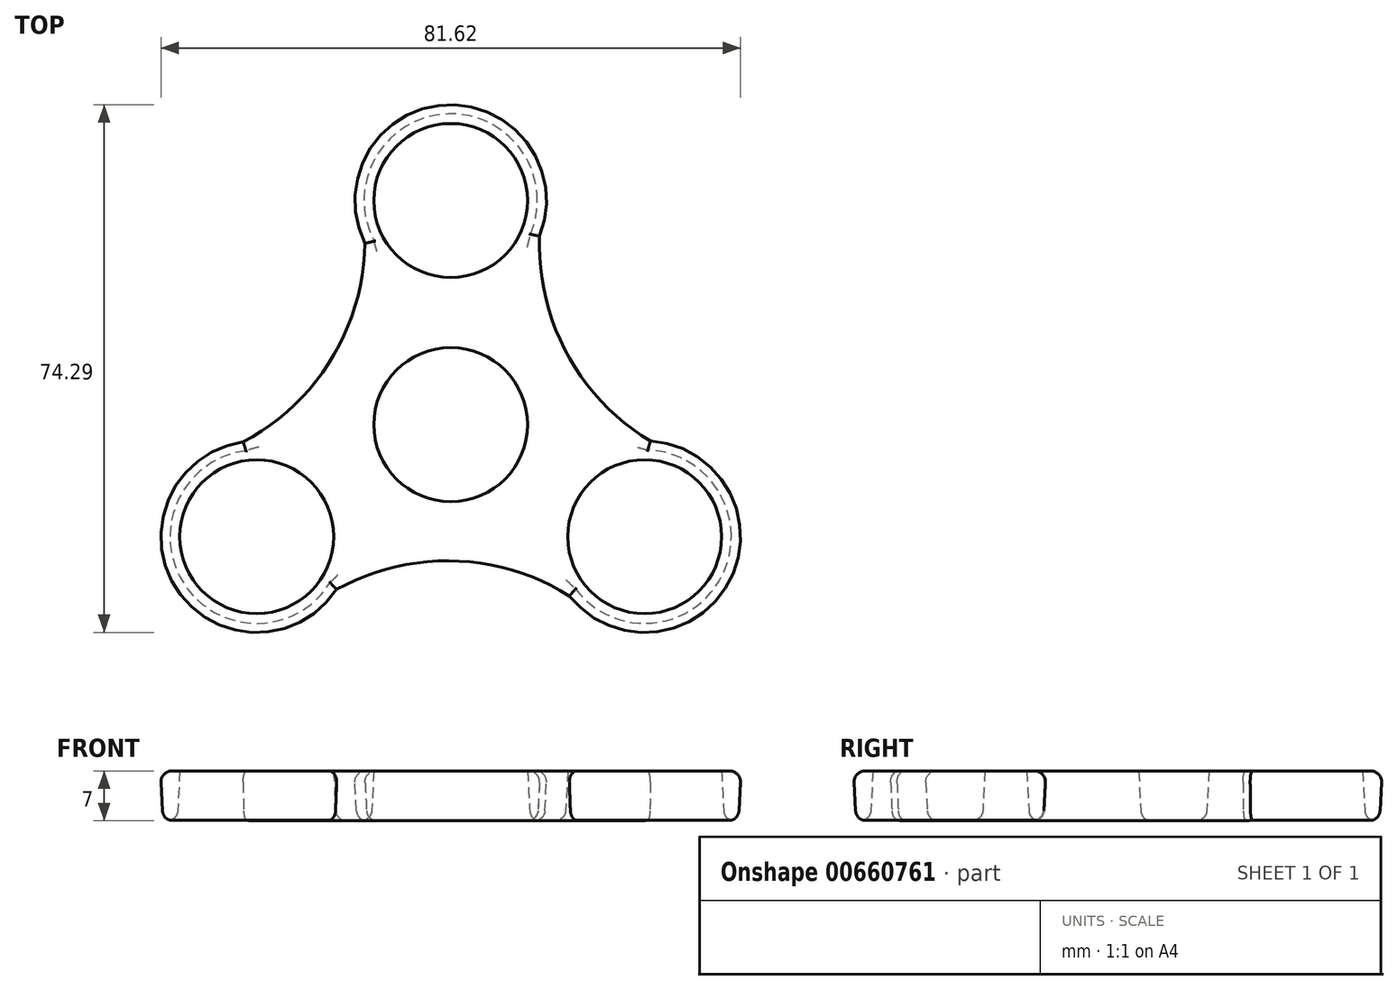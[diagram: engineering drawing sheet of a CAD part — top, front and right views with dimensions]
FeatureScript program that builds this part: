
annotation { "Feature Type Name" : "Feature", "Feature Type Description" : "" }
export const myFeature = defineFeature(function(context is Context, id is Id, definition is map)
    precondition{}
    {
        {
            var Q0;
            Q0=qCreatedBy(makeId("Top.planeOp"),FACE);
            var sketch = newSketch(context, id + "F0", { "sketchPlane" : qUnion([Q0])});
            skCircle(sketch, "E0", {"center": v(0, 0) * mm, "radius": 11.2 * mm});
            skCircle(sketch, "E1", {"center": v(0, 31.55) * mm, "radius": 11.2 * mm});
            skArc(sketch, "E2", {"start": v(12.23, 26.58) * mm, "mid": v(-0.55, 44.74) * mm, "end": v(-11.78, 25.58) * mm});
            skCircle(sketch, "E3.1.0", {"center": v(-27.32, -15.77) * mm, "radius": 11.2 * mm});
            skArc(sketch, "E3.1.1", {"start": v(-29.14, -2.7) * mm, "mid": v(-38.47, -22.84) * mm, "end": v(-16.27, -22.99) * mm});
            skCircle(sketch, "E3.2.0", {"center": v(27.32, -15.77) * mm, "radius": 11.2 * mm});
            skArc(sketch, "E3.2.1", {"start": v(16.9, -23.88) * mm, "mid": v(39.02, -21.9) * mm, "end": v(28.04, -2.6) * mm});
            skArc(sketch, "E4", {"start": v(12.23, 26.58) * mm, "mid": v(16.14, 9.83) * mm, "end": v(28.04, -2.6) * mm});
            skArc(sketch, "E5.1.0", {"start": v(-29.14, -2.7) * mm, "mid": v(-16.58, 9.06) * mm, "end": v(-11.78, 25.58) * mm});
            skArc(sketch, "E5.2.0", {"start": v(16.9, -23.88) * mm, "mid": v(0.44, -18.9) * mm, "end": v(-16.27, -22.99) * mm});
            skSolve(sketch);
        }
        {
            var Q0;
            Q0=makeQuery(id+"F0.imprint","IMPRINT",FACE,{"disambiguationData":[TD([[makeQuery(id+"F0.imprint","IMPRINT",EDGE,{"derivedFrom":sQuery(id+"F0.wireOp",EDGE,"E0")}),-1.0]])]});
            extrude(context, id + "F1", {"entities" : qUnion([Q0]), "depth" : 7 * mm, "offsetDistance" : 25 * mm, "hasDraft" : true, "draftAngle" : 3 * degree});
        }
        {
            var Q0;
            Q0=makeQuery(id+"F1.opExtrude","CAP_EDGE",EDGE,{"disambiguationData":[OSD([sQuery(id+"F0.wireOp",EDGE,"E2")])],"isStart":false});
            var Q1;
            Q1=makeQuery(id+"F1.opExtrude","CAP_EDGE",EDGE,{"disambiguationData":[OSD([sQuery(id+"F0.wireOp",EDGE,"E5.1.0")])],"isStart":false});
            var Q2;
            Q2=makeQuery(id+"F1.opExtrude","CAP_EDGE",EDGE,{"disambiguationData":[OSD([sQuery(id+"F0.wireOp",EDGE,"E3.1.1")])],"isStart":false});
            var Q3;
            Q3=makeQuery(id+"F1.opExtrude","CAP_EDGE",EDGE,{"disambiguationData":[OSD([sQuery(id+"F0.wireOp",EDGE,"E5.2.0")])],"isStart":false});
            var Q4;
            Q4=makeQuery(id+"F1.opExtrude","CAP_EDGE",EDGE,{"disambiguationData":[OSD([sQuery(id+"F0.wireOp",EDGE,"E3.2.1")])],"isStart":false});
            var Q5;
            Q5=makeQuery(id+"F1.opExtrude","CAP_EDGE",EDGE,{"disambiguationData":[OSD([sQuery(id+"F0.wireOp",EDGE,"E4")])],"isStart":false});
            var Q6;
            Q6=makeQuery(id+"F1.opExtrude","CAP_FACE",FACE,{"disambiguationData":[OSD([sQuery(id+"F0.wireOp",EDGE,"E0"),sQuery(id+"F0.wireOp",EDGE,"E1"),sQuery(id+"F0.wireOp",EDGE,"E2"),sQuery(id+"F0.wireOp",EDGE,"E3.1.0"),sQuery(id+"F0.wireOp",EDGE,"E3.1.1"),sQuery(id+"F0.wireOp",EDGE,"E3.2.0"),sQuery(id+"F0.wireOp",EDGE,"E3.2.1"),sQuery(id+"F0.wireOp",EDGE,"E4"),sQuery(id+"F0.wireOp",EDGE,"E5.1.0"),sQuery(id+"F0.wireOp",EDGE,"E5.2.0")])],"isStart":true});
            fillet(context, id + "F2", {"entities" : qUnion([Q0, Q1, Q2, Q3, Q4, Q5, Q6]), "radius" : 1.5 * mm, "tangentPropagation" : true, "allowEdgeOverflow" : false});
        }
    });
